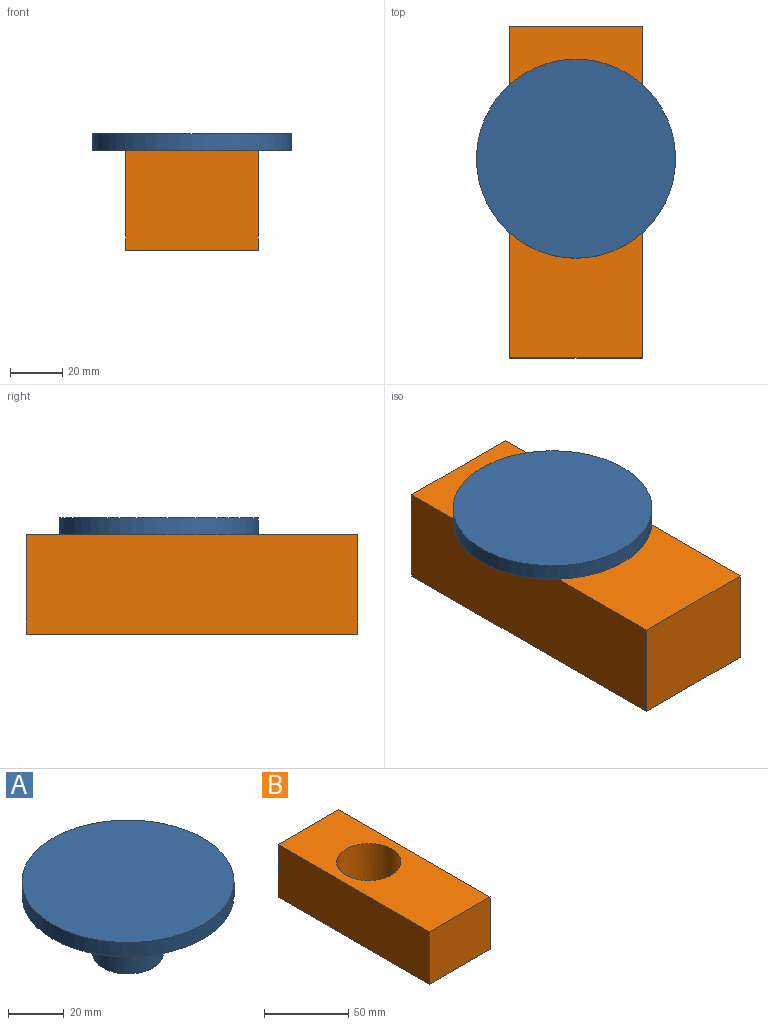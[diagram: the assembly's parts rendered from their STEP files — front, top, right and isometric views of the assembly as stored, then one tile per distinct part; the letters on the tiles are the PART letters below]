
ASSEMBLY  parts=2 mates=1
PART A: 5 faces, bbox 76.2x76.2x31.8 mm
  f0: plane 25.4x25.4mm, normal (0,0,-1), area 506.7mm2, adj f1
  f1: cylinder r=12.7mm len=25.4mm, axis (0,0,-1), area 2026.8mm2, adj f0,f2
  f2: plane 76.2x76.2mm, normal (0,0,-1), area 4053.7mm2, adj f1,f3
  f3: cylinder r=38.1mm len=76.2mm, axis (0,0,-1), area 1520.1mm2, adj f2,f4
  f4: plane 76.2x76.2mm, normal (0,0,1), area 4560.4mm2, adj f3
PART B: 7 faces, bbox 50.8x127x38.1 mm
  f0: plane 127x38.1mm, normal (-1,0,0), area 4838.7mm2, adj f1,f3,f4,f5
  f1: plane 127x50.8mm, normal (0,0,-1), area 5311.5mm2, adj f0,f2,f4,f5,f6
  f2: plane 127x38.1mm, normal (1,0,0), area 4838.7mm2, adj f1,f3,f4,f5
  f3: plane 127x50.8mm, normal (0,0,1), area 5311.5mm2, adj f0,f2,f4,f5,f6
  f4: plane 50.8x38.1mm, normal (0,1,0), area 1935.5mm2, adj f0,f1,f2,f3
  f5: plane 50.8x38.1mm, normal (0,-1,0), area 1935.5mm2, adj f0,f1,f2,f3
  f6: cylinder r=19.05mm len=38.1mm, axis (0,0,1), area 4560.4mm2, adj f1,f3
PLACE A rot(axis=(0,0,1),90deg) t=(25.4,76.2,12.7)mm
PLACE B at identity fixed
MATE fastened A.f1 <-> B.f6  axis (0,0,-1) through (25.4,76.2,38.1)mm
